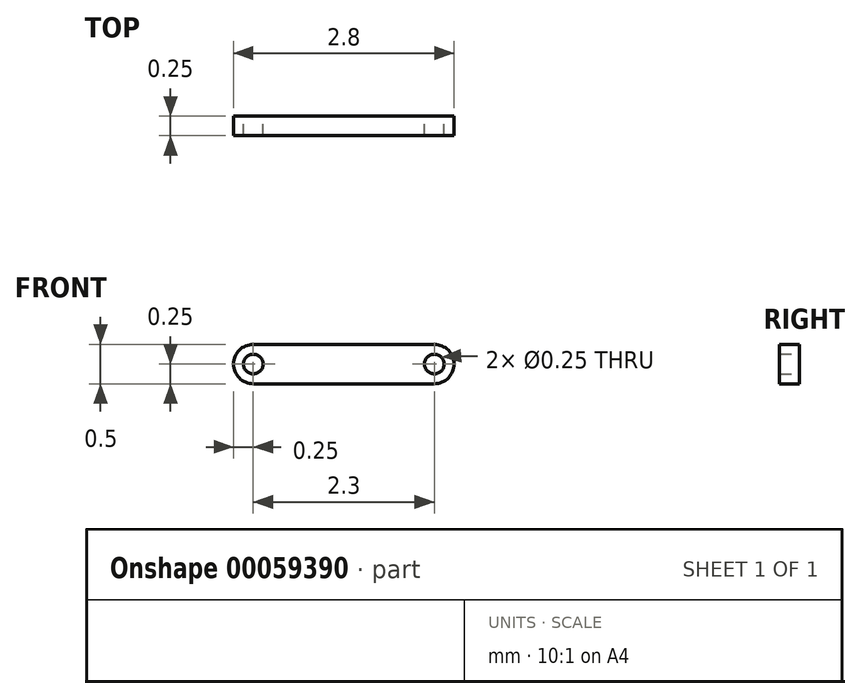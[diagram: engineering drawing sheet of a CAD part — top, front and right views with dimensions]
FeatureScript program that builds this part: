
annotation { "Feature Type Name" : "Feature", "Feature Type Description" : "" }
export const myFeature = defineFeature(function(context is Context, id is Id, definition is map)
    precondition{}
    {
        {
            var Q0;
            Q0=qCreatedBy(makeId("Front.planeOp"),FACE);
            var sketch = newSketch(context, id + "F0", { "sketchPlane" : qUnion([Q0])});
            skCircle(sketch, "E0", {"center": v(0, 0) * mm, "radius": 0.12 * mm});
            skCircle(sketch, "E1", {"center": v(2.3, 0) * mm, "radius": 0.12 * mm});
            skArc(sketch, "E2", {"start": v(2.3, -0.25) * mm, "mid": v(2.55, 0) * mm, "end": v(2.3, 0.25) * mm});
            skArc(sketch, "E3", {"start": v(0, 0.25) * mm, "mid": v(-0.25, 0) * mm, "end": v(0, -0.25) * mm});
            skLineSegment(sketch, "E4", {"start": v(0, 0.25) * mm, "end": v(2.3, 0.25) * mm});
            skLineSegment(sketch, "E5", {"start": v(2.3, -0.25) * mm, "end": v(0, -0.25) * mm});
            skSolve(sketch);
        }
        {
            var Q0;
            Q0=makeQuery(id+"F0.imprint","IMPRINT",FACE,{"disambiguationData":[TD([[makeQuery(id+"F0.imprint","IMPRINT",EDGE,{"derivedFrom":sQuery(id+"F0.wireOp",EDGE,"E0")}),-1.0]])]});
            extrude(context, id + "F1", {"entities" : qUnion([Q0]), "depth" : 0.25 * mm});
        }
    });
